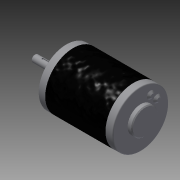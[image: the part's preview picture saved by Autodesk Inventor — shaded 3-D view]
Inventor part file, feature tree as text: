
AUTODESK INVENTOR PART (.ipt)
format: ipt  version: 2014 (Build 180170000, 170)  size: 166,400 bytes
history: native  units: in
note: dims shown in document units (in); Inventor stores cm internally (conversion verified against a paired STEP export)
features: chamfer x1, other x1, imported_body x1
ambient origin geometry x8: Origin, YZ Plane, XZ Plane, XY Plane, X Axis, Y Axis, Z Axis, Center Point
bodies: Body1 (feature_tree)
feature tree (3):
  chamfer  "Chamfer3"  [1 undecoded]
  other  "217-3371-STEP1"
  imported_body  "Base1"
note: 1 required parameter value undecoded (feature->parameter linkage not recoverable at this tier; creation-order binding heuristic only, values carry confidence <= 0.55)
